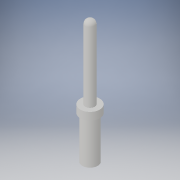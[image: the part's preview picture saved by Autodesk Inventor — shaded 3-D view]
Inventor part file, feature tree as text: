
AUTODESK INVENTOR PART (.ipt)
format: ipt  version: 2019 (Build 230136000, 136)  size: 115,712 bytes
history: native  units: in
note: dims shown in document units (in); Inventor stores cm internally (conversion verified against a paired STEP export)
features: extrude x3, sketch x3, projected_geometry x2, fillet x1
ambient origin geometry x8: Origin, YZ Plane, XZ Plane, XY Plane, X Axis, Y Axis, Z Axis, Center Point
bodies: Solid1 (feature_tree)
feature tree (9):
  extrude  "Extrusion1"  Depth=0.185in TaperAngle=0.0deg
  extrude  "Extrusion2"  Depth=0.033in TaperAngle=0.0deg
  extrude  "Extrusion3"  Depth=0.325in TaperAngle=0.0deg
  fillet  "Fillet1"  Radius=0.02in
  sketch  "Sketch1"  dims[d0=0.067in d1=0.185in d2=0.0in]
  sketch  "Sketch2"  dims[d3=0.085in d4=0.033in d5=0.0in]
  projected_geometry  "Projected Loop1"
  sketch  "Sketch3"  dims[d6=0.041in d7=0.325in d8=0.0in d9=0.02in]
  projected_geometry  "Projected Loop2"
